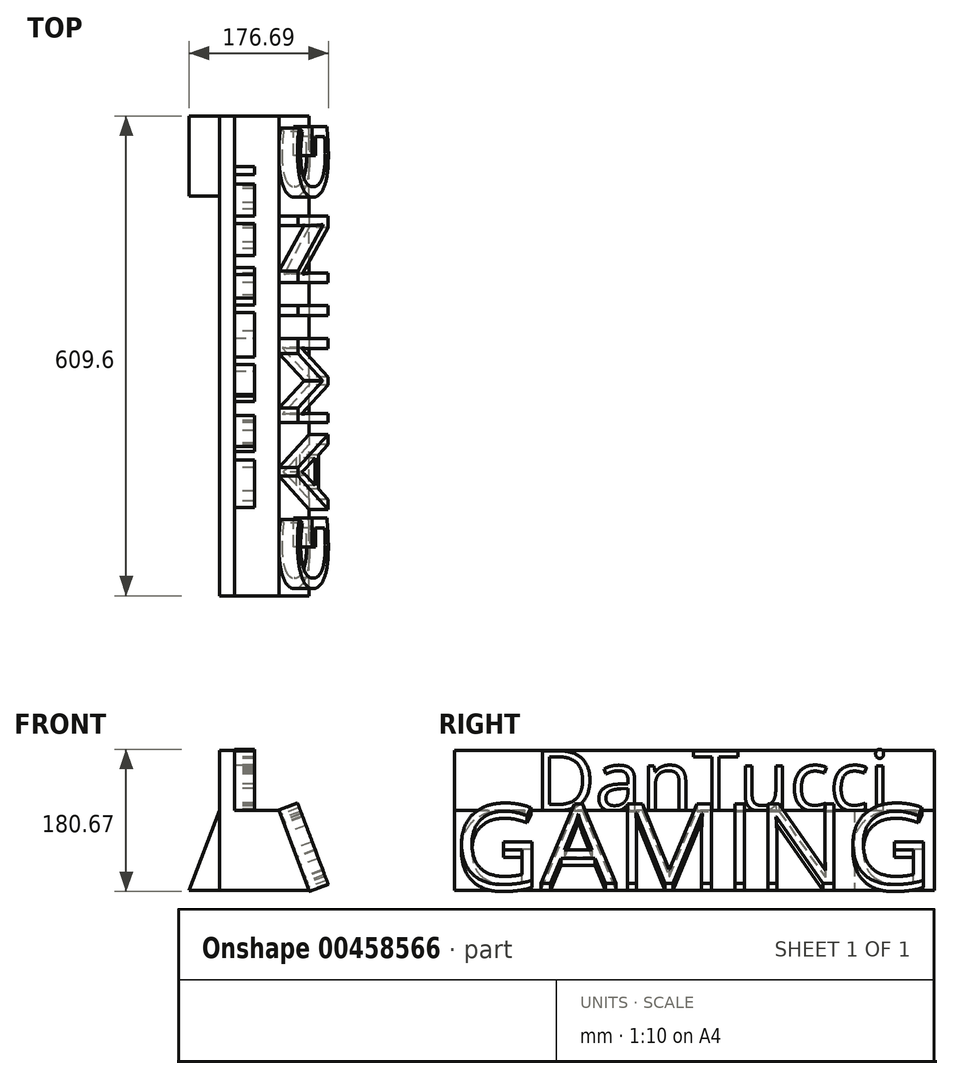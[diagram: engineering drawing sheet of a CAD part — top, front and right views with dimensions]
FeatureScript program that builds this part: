
annotation { "Feature Type Name" : "Feature", "Feature Type Description" : "" }
export const myFeature = defineFeature(function(context is Context, id is Id, definition is map)
    precondition{}
    {
        {
            var Q0;
            Q0=qCreatedBy(makeId("Front.planeOp"),FACE);
            var sketch = newSketch(context, id + "F0", { "sketchPlane" : qUnion([Q0])});
            skLineSegment(sketch, "E0", {"start": v(0, -100.2) * mm, "end": v(0, -201.8) * mm});
            skLineSegment(sketch, "E1", {"start": v(-37.84, -100.2) * mm, "end": v(-76.2, -201.8) * mm});
            skLineSegment(sketch, "E2", {"start": v(-76.2, -201.8) * mm, "end": v(0, -201.8) * mm});
            skLineSegment(sketch, "E3.MirrorCS", {"start": v(76.2, -201.8) * mm, "end": v(0, -201.8) * mm});
            skLineSegment(sketch, "E4.MirrorCS", {"start": v(37.84, -100.2) * mm, "end": v(76.2, -201.8) * mm});
            skLineSegment(sketch, "E5", {"start": v(-37.84, -100.2) * mm, "end": v(37.84, -100.2) * mm});
            skPoint(sketch, "E6.orphan", {"position": v(0, 0) * mm});
            skPoint(sketch, "E7.orphan", {"position": v(76.2, -100.2) * mm});
            skSolve(sketch);
        }
        {
            var Q0;
            Q0 = qSketchRegion(id + "F0", true);
            extrude(context, id + "F1", {"entities" : qUnion([Q0]), "depth" : 609.6 * mm});
        }
        {
            var Q0;
            Q0=makeQuery(id+"F1.opExtrude","SWEPT_FACE",FACE,{"disambiguationData":[OSD([sQuery(id+"F0.wireOp",EDGE,"E5")])]});
            var sketch = newSketch(context, id + "F2", { "sketchPlane" : qUnion([Q0])});
            skLineSegment(sketch, "E8", {"start": v(0, -609.6) * mm, "end": v(-37.84, -609.6) * mm});
            skLineSegment(sketch, "E9", {"start": v(-37.84, -609.6) * mm, "end": v(-18.92, -609.6) * mm});
            skLineSegment(sketch, "E10", {"start": v(-18.92, -609.6) * mm, "end": v(-18.92, 0) * mm});
            skLineSegment(sketch, "E11", {"start": v(-18.92, 0) * mm, "end": v(-37.84, 0) * mm});
            skLineSegment(sketch, "E12", {"start": v(-37.84, 0) * mm, "end": v(-37.84, -609.6) * mm});
            skSolve(sketch);
        }
        {
            var Q0;
            Q0 = qSketchRegion(id + "F2", true);
            extrude(context, id + "F3", {"entities" : qUnion([Q0]), "operationType" : NewBodyOperationType.ADD, "depth" : 76.2 * mm});
        }
        {
            var Q0;
            Q0=makeQuery(id+"F3.boolean.opBoolean","MERGE",FACE,{"derivedFrom":[makeQuery(id+"F1.opExtrude","CAP_FACE",FACE,{"disambiguationData":[OSD([sQuery(id+"F0.wireOp",EDGE,"E1"),sQuery(id+"F0.wireOp",EDGE,"E2"),sQuery(id+"F0.wireOp",EDGE,"E3.MirrorCS"),sQuery(id+"F0.wireOp",EDGE,"E4.MirrorCS"),sQuery(id+"F0.wireOp",EDGE,"E5")])],"isStart":false}),makeQuery(id+"F3.opExtrude","SWEPT_FACE",FACE,{"disambiguationData":[OSD([sQuery(id+"F2.wireOp",EDGE,"E9")])]})]});
            var sketch = newSketch(context, id + "F4", { "sketchPlane" : qUnion([Q0])});
            skLineSegment(sketch, "E13", {"start": v(-37.84, -100.2) * mm, "end": v(-37.84, -201.8) * mm});
            skLineSegment(sketch, "E14.0", {"start": v(-37.84, -100.2) * mm, "end": v(-76.2, -201.8) * mm});
            skLineSegment(sketch, "E15.0", {"start": v(-76.2, -201.8) * mm, "end": v(76.2, -201.8) * mm});
            skSolve(sketch);
        }
        {
            var Q0;
            Q0 = qSketchRegion(id + "F4", true);
            extrude(context, id + "F5", {"entities" : qUnion([Q0]), "operationType" : NewBodyOperationType.REMOVE, "oppositeDirection" : true, "depth" : 508 * mm});
        }
        {
            var Q0;
            Q0=makeQuery(id+"F3.opExtrude","SWEPT_FACE",FACE,{"disambiguationData":[OSD([sQuery(id+"F2.wireOp",EDGE,"E10")])]});
            var sketch = newSketch(context, id + "F6", { "sketchPlane" : qUnion([Q0])});
            skText(sketch, "E16", { "text": "DanTucci", "fontName": "OpenSans-Regular.ttf"});
            const initialGuessF6  = {"E16": [-0.508, -0.1002, 1, 0, 0.0762]};
            skSetInitialGuess(sketch, initialGuessF6);
            skSolve(sketch);
        }
        {
            var Q0;
            Q0 = qSketchRegion(id + "F6", true);
            extrude(context, id + "F7", {"entities" : qUnion([Q0]), "operationType" : NewBodyOperationType.ADD, "depth" : 25.4 * mm});
        }
        {
            var Q0;
            Q0=makeQuery(id+"F1.opExtrude","SWEPT_FACE",FACE,{"disambiguationData":[OSD([sQuery(id+"F0.wireOp",EDGE,"E4.MirrorCS")])]});
            var sketch = newSketch(context, id + "F8", { "sketchPlane" : qUnion([Q0])});
            skText(sketch, "E17", { "text": "GAMING\n", "fontName": "OpenSans-Regular.ttf"});
            const initialGuessF8  = {"E17": [-0.6096, -0.21572, 1, 0, 0.1086]};
            skSetInitialGuess(sketch, initialGuessF8);
            skSolve(sketch);
        }
        {
            var Q0;
            Q0 = qSketchRegion(id + "F8", true);
            extrude(context, id + "F9", {"entities" : qUnion([Q0]), "operationType" : NewBodyOperationType.ADD, "depth" : 25.4 * mm});
        }
    });
